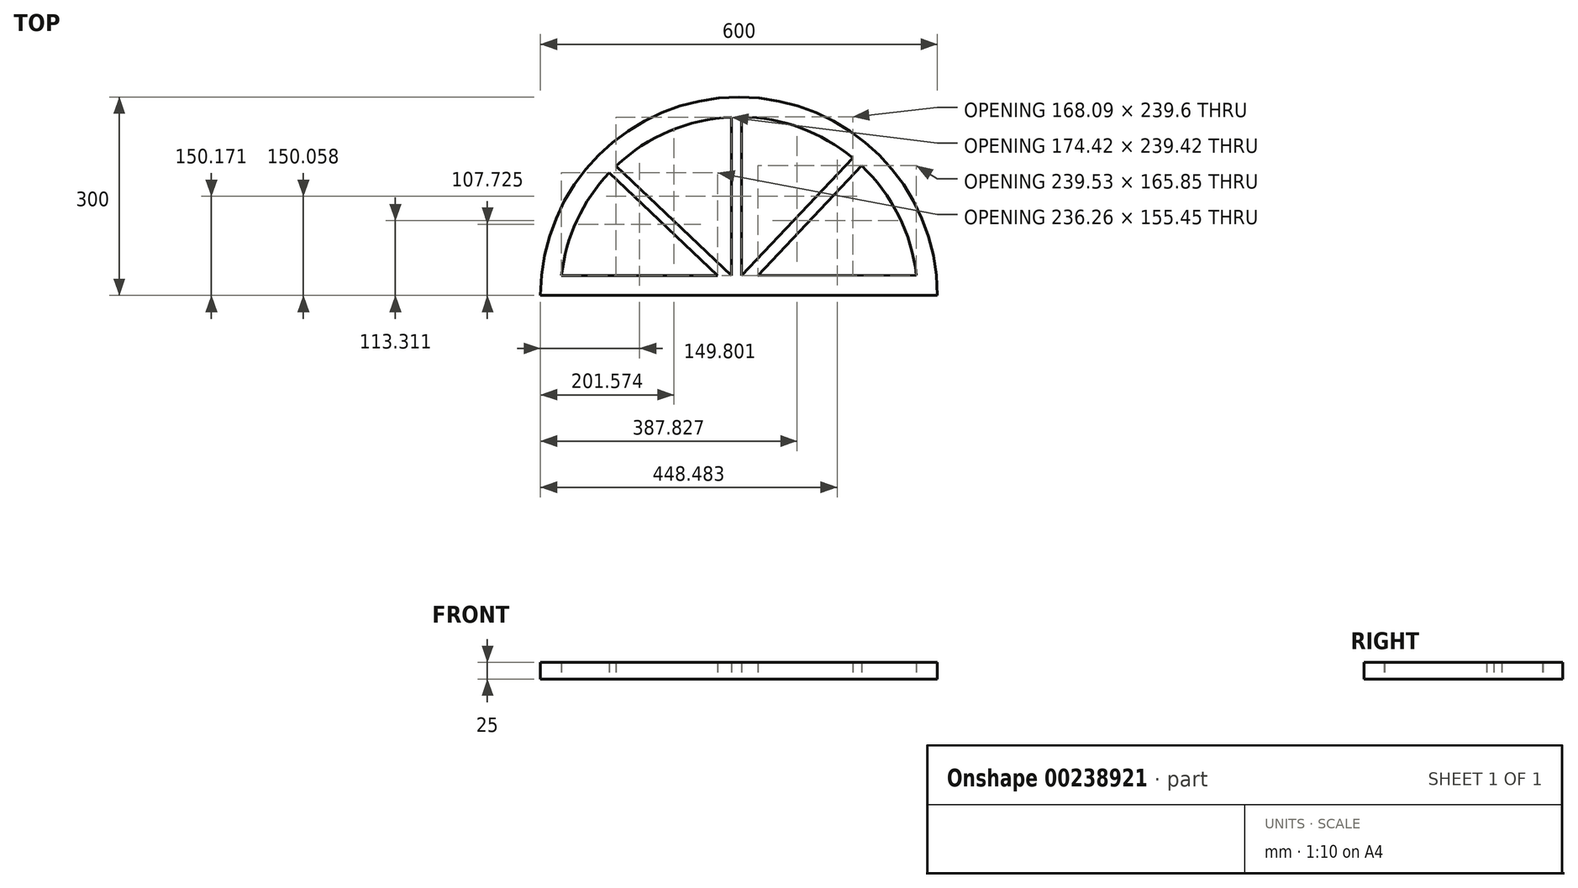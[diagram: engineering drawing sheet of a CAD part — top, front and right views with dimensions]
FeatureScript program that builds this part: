
annotation { "Feature Type Name" : "Feature", "Feature Type Description" : "" }
export const myFeature = defineFeature(function(context is Context, id is Id, definition is map)
    precondition{}
    {
        {
            var Q0;
            Q0=qCreatedBy(makeId("Top.planeOp"),FACE);
            var sketch = newSketch(context, id + "F0", { "sketchPlane" : qUnion([Q0])});
            skArc(sketch, "E0", {"start": v(300, 0) * mm, "mid": v(0, 300) * mm, "end": v(-300, 0) * mm});
            skArc(sketch, "E1", {"start": v(268.25, 30.7) * mm, "mid": v(241.48, 120.78) * mm, "end": v(185.45, 196.24) * mm});
            skLineSegment(sketch, "E2", {"start": v(0, 0) * mm, "end": v(300, 0) * mm});
            skLineSegment(sketch, "E3", {"start": v(300, 0) * mm, "end": v(0, 0) * mm});
            skLineSegment(sketch, "E4", {"start": v(0, 0) * mm, "end": v(-300, 0) * mm});
            skLineSegment(sketch, "E5", {"start": v(-300, 0) * mm, "end": v(0, 0) * mm});
            skLineSegment(sketch, "E6", {"start": v(28.72, 30.39) * mm, "end": v(185.45, 196.24) * mm});
            skLineSegment(sketch, "E7", {"start": v(185.45, 196.24) * mm, "end": v(28.72, 30.39) * mm});
            skLineSegment(sketch, "E8", {"start": v(-32.07, 30.3) * mm, "end": v(-196.24, 185.45) * mm});
            skLineSegment(sketch, "E9", {"start": v(-196.24, 185.45) * mm, "end": v(-32.07, 30.3) * mm});
            skLineSegment(sketch, "E10", {"start": v(-299.71, 29.96) * mm, "end": v(-298.5, 29.96) * mm});
            skPoint(sketch, "E11.orphan", {"position": v(0, 300) * mm});
            skLineSegment(sketch, "E12.trimOffspring", {"start": v(-268.33, 30) * mm, "end": v(-32.07, 30.3) * mm});
            skLineSegment(sketch, "E13.trimOffspring", {"start": v(298.42, 30.74) * mm, "end": v(300.29, 30.74) * mm});
            skArc(sketch, "E14.trimOffspring", {"start": v(-196.24, 185.45) * mm, "mid": v(-244.94, 113.6) * mm, "end": v(-268.33, 30) * mm});
            skLineSegment(sketch, "E15.trimOffspring", {"start": v(28.72, 30.39) * mm, "end": v(268.25, 30.7) * mm});
            skLineSegment(sketch, "E16", {"start": v(-185.63, 196.06) * mm, "end": v(-11.22, 30.35) * mm});
            skLineSegment(sketch, "E17", {"start": v(-11.22, 269.77) * mm, "end": v(-11.22, 30.35) * mm});
            skLineSegment(sketch, "E18", {"start": v(3.78, 30.37) * mm, "end": v(3.78, 269.97) * mm});
            skLineSegment(sketch, "E19", {"start": v(3.78, 30.37) * mm, "end": v(171.87, 208.23) * mm});
            skArc(sketch, "E20.trimOffspring", {"start": v(-11.22, 269.77) * mm, "mid": v(-105.1, 248.7) * mm, "end": v(-185.63, 196.06) * mm});
            skArc(sketch, "E21.trimOffspring", {"start": v(171.87, 208.23) * mm, "mid": v(93.1, 253.44) * mm, "end": v(3.78, 269.97) * mm});
            skSolve(sketch);
        }
        {
            var Q0;
            Q0 = qSketchRegion(id + "F0", true);
            extrude(context, id + "F1", {"entities" : qUnion([Q0]), "depth" : 25 * mm});
        }
    });
